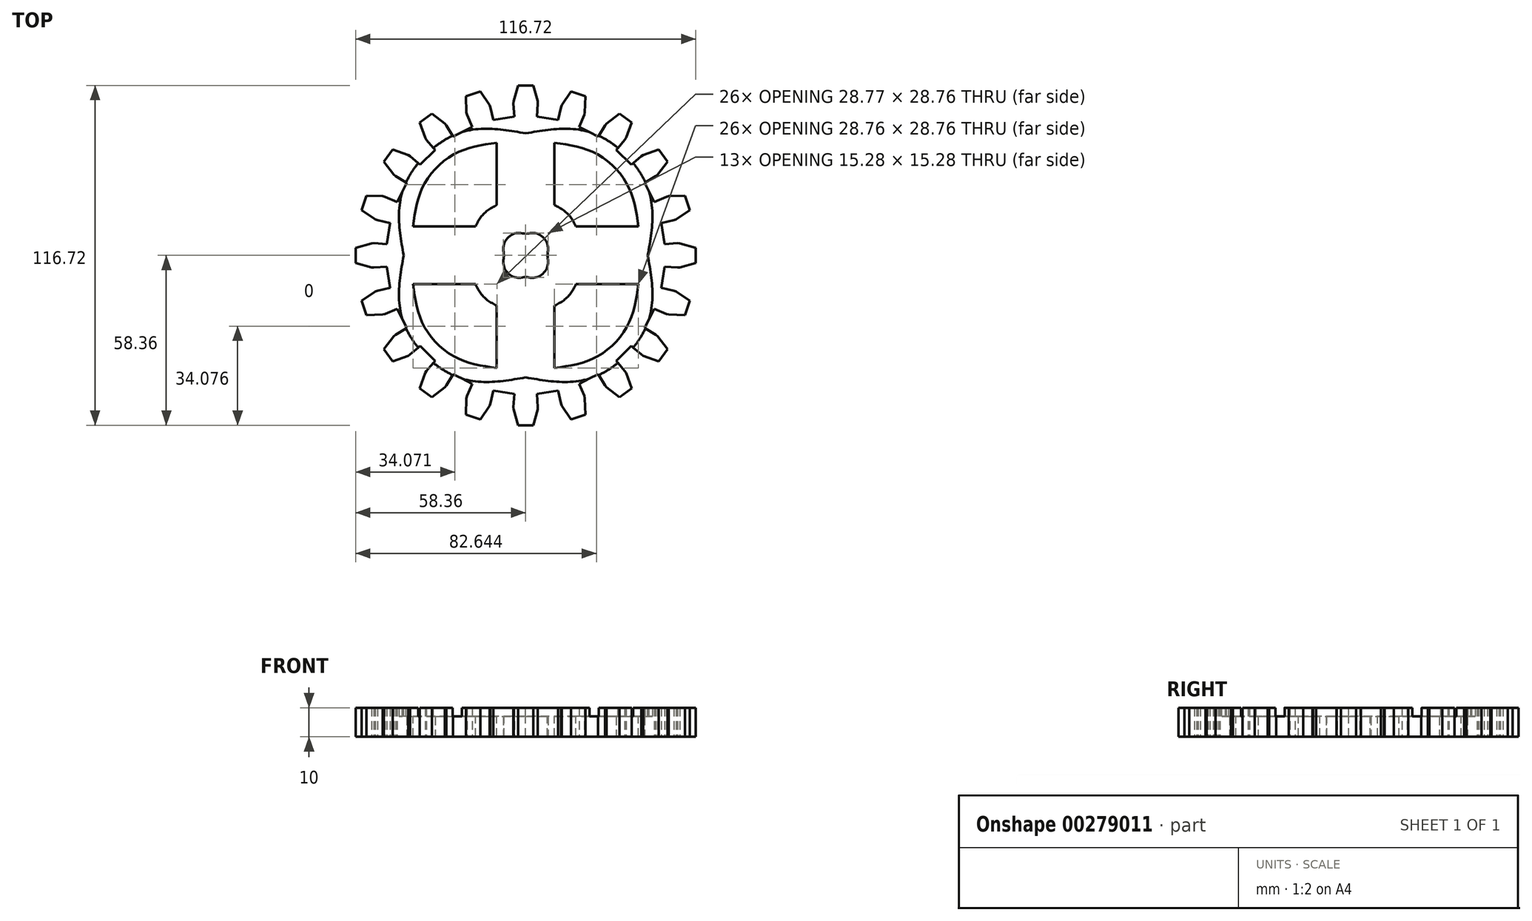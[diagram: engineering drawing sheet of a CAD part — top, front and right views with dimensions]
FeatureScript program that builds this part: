
annotation { "Feature Type Name" : "Feature", "Feature Type Description" : "" }
export const myFeature = defineFeature(function(context is Context, id is Id, definition is map)
    precondition{}
    {
        {
            var Q0;
            Q0=qCreatedBy(makeId("Top.planeOp"),FACE);
            var sketch = newSketch(context, id + "F0", { "sketchPlane" : qUnion([Q0])});
            skLineSegment(sketch, "E0", {"start": v(-2.6, 58.36) * mm, "end": v(-4.17, 52.94) * mm});
            skLineSegment(sketch, "E1", {"start": v(-4.17, 52.94) * mm, "end": v(-4.2, 52.13) * mm});
            skLineSegment(sketch, "E2", {"start": v(-4.2, 52.13) * mm, "end": v(-3.84, 47.64) * mm});
            skLineSegment(sketch, "E3", {"start": v(-3.84, 47.64) * mm, "end": v(-11.08, 46.5) * mm});
            skLineSegment(sketch, "E4", {"start": v(-11.08, 46.5) * mm, "end": v(-12.12, 50.88) * mm});
            skLineSegment(sketch, "E5", {"start": v(-12.12, 50.88) * mm, "end": v(-12.4, 51.64) * mm});
            skLineSegment(sketch, "E6", {"start": v(-12.4, 51.64) * mm, "end": v(-15.57, 56.3) * mm});
            skLineSegment(sketch, "E7", {"start": v(-15.57, 56.3) * mm, "end": v(-20.5, 54.7) * mm});
            skLineSegment(sketch, "E8", {"start": v(-20.5, 54.7) * mm, "end": v(-20.33, 49.06) * mm});
            skLineSegment(sketch, "E9", {"start": v(-20.33, 49.06) * mm, "end": v(-20.1, 48.29) * mm});
            skLineSegment(sketch, "E10", {"start": v(-20.1, 48.29) * mm, "end": v(-18.37, 44.12) * mm});
            skLineSegment(sketch, "E11", {"start": v(-18.37, 44.12) * mm, "end": v(-24.9, 40.8) * mm});
            skLineSegment(sketch, "E12", {"start": v(-24.9, 40.8) * mm, "end": v(-27.25, 44.64) * mm});
            skLineSegment(sketch, "E13", {"start": v(-27.25, 44.64) * mm, "end": v(-27.75, 45.28) * mm});
            skLineSegment(sketch, "E14", {"start": v(-27.75, 45.28) * mm, "end": v(-32.2, 48.74) * mm});
            skLineSegment(sketch, "E15", {"start": v(-32.2, 48.74) * mm, "end": v(-36.4, 45.68) * mm});
            skLineSegment(sketch, "E16", {"start": v(-36.4, 45.68) * mm, "end": v(-34.5, 40.38) * mm});
            skLineSegment(sketch, "E17", {"start": v(-34.5, 40.38) * mm, "end": v(-34.04, 39.7) * mm});
            skLineSegment(sketch, "E18", {"start": v(-34.04, 39.7) * mm, "end": v(-31.1, 36.3) * mm});
            skLineSegment(sketch, "E19", {"start": v(-31.1, 36.3) * mm, "end": v(-36.3, 31.1) * mm});
            skLineSegment(sketch, "E20", {"start": v(-36.3, 31.1) * mm, "end": v(-39.71, 34.03) * mm});
            skLineSegment(sketch, "E21", {"start": v(-39.71, 34.03) * mm, "end": v(-40.38, 34.5) * mm});
            skLineSegment(sketch, "E22", {"start": v(-40.38, 34.5) * mm, "end": v(-45.7, 36.4) * mm});
            skLineSegment(sketch, "E23", {"start": v(-45.7, 36.4) * mm, "end": v(-48.75, 32.2) * mm});
            skLineSegment(sketch, "E24", {"start": v(-48.75, 32.2) * mm, "end": v(-45.29, 27.75) * mm});
            skLineSegment(sketch, "E25", {"start": v(-45.29, 27.75) * mm, "end": v(-44.64, 27.24) * mm});
            skLineSegment(sketch, "E26", {"start": v(-44.64, 27.24) * mm, "end": v(-40.8, 24.9) * mm});
            skLineSegment(sketch, "E27", {"start": v(-40.8, 24.9) * mm, "end": v(-44.12, 18.37) * mm});
            skLineSegment(sketch, "E28", {"start": v(-44.12, 18.37) * mm, "end": v(-48.29, 20.1) * mm});
            skLineSegment(sketch, "E29", {"start": v(-48.29, 20.1) * mm, "end": v(-49.07, 20.32) * mm});
            skLineSegment(sketch, "E30", {"start": v(-49.07, 20.32) * mm, "end": v(-54.7, 20.5) * mm});
            skLineSegment(sketch, "E31", {"start": v(-54.7, 20.5) * mm, "end": v(-56.31, 15.57) * mm});
            skLineSegment(sketch, "E32", {"start": v(-56.31, 15.57) * mm, "end": v(-51.65, 12.4) * mm});
            skLineSegment(sketch, "E33", {"start": v(-51.65, 12.4) * mm, "end": v(-50.88, 12.12) * mm});
            skLineSegment(sketch, "E34", {"start": v(-50.88, 12.12) * mm, "end": v(-46.5, 11.08) * mm});
            skLineSegment(sketch, "E35", {"start": v(-46.5, 11.08) * mm, "end": v(-47.64, 3.84) * mm});
            skLineSegment(sketch, "E36", {"start": v(-47.64, 3.84) * mm, "end": v(-52.13, 4.2) * mm});
            skLineSegment(sketch, "E37", {"start": v(-52.13, 4.2) * mm, "end": v(-52.94, 4.16) * mm});
            skLineSegment(sketch, "E38", {"start": v(-52.94, 4.16) * mm, "end": v(-58.36, 2.6) * mm});
            skLineSegment(sketch, "E39", {"start": v(-58.36, 2.6) * mm, "end": v(-58.36, -2.6) * mm});
            skLineSegment(sketch, "E40", {"start": v(-58.36, -2.6) * mm, "end": v(-52.94, -4.16) * mm});
            skLineSegment(sketch, "E41", {"start": v(-52.94, -4.16) * mm, "end": v(-52.13, -4.2) * mm});
            skLineSegment(sketch, "E42", {"start": v(-52.13, -4.2) * mm, "end": v(-47.64, -3.84) * mm});
            skLineSegment(sketch, "E43", {"start": v(-47.64, -3.84) * mm, "end": v(-46.5, -11.08) * mm});
            skLineSegment(sketch, "E44", {"start": v(-46.5, -11.08) * mm, "end": v(-50.88, -12.12) * mm});
            skLineSegment(sketch, "E45", {"start": v(-50.88, -12.12) * mm, "end": v(-51.65, -12.4) * mm});
            skLineSegment(sketch, "E46", {"start": v(-51.65, -12.4) * mm, "end": v(-56.31, -15.57) * mm});
            skLineSegment(sketch, "E47", {"start": v(-56.31, -15.57) * mm, "end": v(-54.7, -20.5) * mm});
            skLineSegment(sketch, "E48", {"start": v(-54.7, -20.5) * mm, "end": v(-49.07, -20.32) * mm});
            skLineSegment(sketch, "E49", {"start": v(-49.07, -20.32) * mm, "end": v(-48.29, -20.1) * mm});
            skLineSegment(sketch, "E50", {"start": v(-48.29, -20.1) * mm, "end": v(-44.12, -18.37) * mm});
            skLineSegment(sketch, "E51", {"start": v(-44.12, -18.37) * mm, "end": v(-40.8, -24.9) * mm});
            skLineSegment(sketch, "E52", {"start": v(-40.8, -24.9) * mm, "end": v(-44.64, -27.24) * mm});
            skLineSegment(sketch, "E53", {"start": v(-44.64, -27.24) * mm, "end": v(-45.29, -27.75) * mm});
            skLineSegment(sketch, "E54", {"start": v(-45.29, -27.75) * mm, "end": v(-48.75, -32.2) * mm});
            skLineSegment(sketch, "E55", {"start": v(-48.75, -32.2) * mm, "end": v(-45.7, -36.4) * mm});
            skLineSegment(sketch, "E56", {"start": v(-45.7, -36.4) * mm, "end": v(-40.38, -34.5) * mm});
            skLineSegment(sketch, "E57", {"start": v(-40.38, -34.5) * mm, "end": v(-39.71, -34.03) * mm});
            skLineSegment(sketch, "E58", {"start": v(-39.71, -34.03) * mm, "end": v(-36.3, -31.1) * mm});
            skLineSegment(sketch, "E59", {"start": v(-36.3, -31.1) * mm, "end": v(-31.1, -36.3) * mm});
            skLineSegment(sketch, "E60", {"start": v(-31.1, -36.3) * mm, "end": v(-34.04, -39.7) * mm});
            skLineSegment(sketch, "E61", {"start": v(-34.04, -39.7) * mm, "end": v(-34.5, -40.38) * mm});
            skLineSegment(sketch, "E62", {"start": v(-34.5, -40.38) * mm, "end": v(-36.4, -45.68) * mm});
            skLineSegment(sketch, "E63", {"start": v(-36.4, -45.68) * mm, "end": v(-32.2, -48.74) * mm});
            skLineSegment(sketch, "E64", {"start": v(-32.2, -48.74) * mm, "end": v(-27.75, -45.28) * mm});
            skLineSegment(sketch, "E65", {"start": v(-27.75, -45.28) * mm, "end": v(-27.25, -44.64) * mm});
            skLineSegment(sketch, "E66", {"start": v(-27.25, -44.64) * mm, "end": v(-24.9, -40.8) * mm});
            skLineSegment(sketch, "E67", {"start": v(-24.9, -40.8) * mm, "end": v(-18.37, -44.12) * mm});
            skLineSegment(sketch, "E68", {"start": v(-18.37, -44.12) * mm, "end": v(-20.1, -48.28) * mm});
            skLineSegment(sketch, "E69", {"start": v(-20.1, -48.28) * mm, "end": v(-20.33, -49.06) * mm});
            skLineSegment(sketch, "E70", {"start": v(-20.33, -49.06) * mm, "end": v(-20.5, -54.7) * mm});
            skLineSegment(sketch, "E71", {"start": v(-20.5, -54.7) * mm, "end": v(-15.57, -56.3) * mm});
            skLineSegment(sketch, "E72", {"start": v(-15.57, -56.3) * mm, "end": v(-12.4, -51.64) * mm});
            skLineSegment(sketch, "E73", {"start": v(-12.4, -51.64) * mm, "end": v(-12.12, -50.88) * mm});
            skLineSegment(sketch, "E74", {"start": v(-12.12, -50.88) * mm, "end": v(-11.08, -46.5) * mm});
            skLineSegment(sketch, "E75", {"start": v(-11.08, -46.5) * mm, "end": v(-3.84, -47.64) * mm});
            skLineSegment(sketch, "E76", {"start": v(-3.84, -47.64) * mm, "end": v(-4.2, -52.13) * mm});
            skLineSegment(sketch, "E77", {"start": v(-4.2, -52.13) * mm, "end": v(-4.17, -52.94) * mm});
            skLineSegment(sketch, "E78", {"start": v(-4.17, -52.94) * mm, "end": v(-2.6, -58.36) * mm});
            skLineSegment(sketch, "E79", {"start": v(-2.6, -58.36) * mm, "end": v(2.6, -58.36) * mm});
            skLineSegment(sketch, "E80", {"start": v(2.6, -58.36) * mm, "end": v(4.16, -52.94) * mm});
            skLineSegment(sketch, "E81", {"start": v(4.16, -52.94) * mm, "end": v(4.19, -52.13) * mm});
            skLineSegment(sketch, "E82", {"start": v(4.19, -52.13) * mm, "end": v(3.83, -47.64) * mm});
            skLineSegment(sketch, "E83", {"start": v(3.83, -47.64) * mm, "end": v(11.07, -46.5) * mm});
            skLineSegment(sketch, "E84", {"start": v(11.07, -46.5) * mm, "end": v(12.12, -50.88) * mm});
            skLineSegment(sketch, "E85", {"start": v(12.12, -50.88) * mm, "end": v(12.4, -51.64) * mm});
            skLineSegment(sketch, "E86", {"start": v(12.4, -51.64) * mm, "end": v(15.56, -56.3) * mm});
            skLineSegment(sketch, "E87", {"start": v(15.56, -56.3) * mm, "end": v(20.5, -54.7) * mm});
            skLineSegment(sketch, "E88", {"start": v(20.5, -54.7) * mm, "end": v(20.32, -49.06) * mm});
            skLineSegment(sketch, "E89", {"start": v(20.32, -49.06) * mm, "end": v(20.1, -48.28) * mm});
            skLineSegment(sketch, "E90", {"start": v(20.1, -48.28) * mm, "end": v(18.36, -44.12) * mm});
            skLineSegment(sketch, "E91", {"start": v(18.36, -44.12) * mm, "end": v(24.9, -40.8) * mm});
            skLineSegment(sketch, "E92", {"start": v(24.9, -40.8) * mm, "end": v(27.24, -44.64) * mm});
            skLineSegment(sketch, "E93", {"start": v(27.24, -44.64) * mm, "end": v(27.75, -45.28) * mm});
            skLineSegment(sketch, "E94", {"start": v(27.75, -45.28) * mm, "end": v(32.2, -48.74) * mm});
            skLineSegment(sketch, "E95", {"start": v(32.2, -48.74) * mm, "end": v(36.4, -45.68) * mm});
            skLineSegment(sketch, "E96", {"start": v(36.4, -45.68) * mm, "end": v(34.48, -40.38) * mm});
            skLineSegment(sketch, "E97", {"start": v(34.48, -40.38) * mm, "end": v(34.03, -39.7) * mm});
            skLineSegment(sketch, "E98", {"start": v(34.03, -39.7) * mm, "end": v(31.1, -36.3) * mm});
            skLineSegment(sketch, "E99", {"start": v(31.1, -36.3) * mm, "end": v(36.28, -31.1) * mm});
            skLineSegment(sketch, "E100", {"start": v(36.28, -31.1) * mm, "end": v(39.7, -34.03) * mm});
            skLineSegment(sketch, "E101", {"start": v(39.7, -34.03) * mm, "end": v(40.38, -34.5) * mm});
            skLineSegment(sketch, "E102", {"start": v(40.38, -34.5) * mm, "end": v(45.68, -36.4) * mm});
            skLineSegment(sketch, "E103", {"start": v(45.68, -36.4) * mm, "end": v(48.74, -32.2) * mm});
            skLineSegment(sketch, "E104", {"start": v(48.74, -32.2) * mm, "end": v(45.28, -27.75) * mm});
            skLineSegment(sketch, "E105", {"start": v(45.28, -27.75) * mm, "end": v(44.64, -27.24) * mm});
            skLineSegment(sketch, "E106", {"start": v(44.64, -27.24) * mm, "end": v(40.79, -24.9) * mm});
            skLineSegment(sketch, "E107", {"start": v(40.79, -24.9) * mm, "end": v(44.12, -18.37) * mm});
            skLineSegment(sketch, "E108", {"start": v(44.12, -18.37) * mm, "end": v(48.28, -20.1) * mm});
            skLineSegment(sketch, "E109", {"start": v(48.28, -20.1) * mm, "end": v(49.06, -20.32) * mm});
            skLineSegment(sketch, "E110", {"start": v(49.06, -20.32) * mm, "end": v(54.7, -20.5) * mm});
            skLineSegment(sketch, "E111", {"start": v(54.7, -20.5) * mm, "end": v(56.3, -15.57) * mm});
            skLineSegment(sketch, "E112", {"start": v(56.3, -15.57) * mm, "end": v(51.64, -12.4) * mm});
            skLineSegment(sketch, "E113", {"start": v(51.64, -12.4) * mm, "end": v(50.87, -12.12) * mm});
            skLineSegment(sketch, "E114", {"start": v(50.87, -12.12) * mm, "end": v(46.49, -11.08) * mm});
            skLineSegment(sketch, "E115", {"start": v(46.49, -11.08) * mm, "end": v(47.63, -3.84) * mm});
            skLineSegment(sketch, "E116", {"start": v(47.63, -3.84) * mm, "end": v(52.12, -4.2) * mm});
            skLineSegment(sketch, "E117", {"start": v(52.12, -4.2) * mm, "end": v(52.94, -4.16) * mm});
            skLineSegment(sketch, "E118", {"start": v(52.94, -4.16) * mm, "end": v(58.36, -2.6) * mm});
            skLineSegment(sketch, "E119", {"start": v(58.36, -2.6) * mm, "end": v(58.36, 2.6) * mm});
            skLineSegment(sketch, "E120", {"start": v(58.36, 2.6) * mm, "end": v(52.94, 4.16) * mm});
            skLineSegment(sketch, "E121", {"start": v(52.94, 4.16) * mm, "end": v(52.12, 4.2) * mm});
            skLineSegment(sketch, "E122", {"start": v(52.12, 4.2) * mm, "end": v(47.63, 3.84) * mm});
            skLineSegment(sketch, "E123", {"start": v(47.63, 3.84) * mm, "end": v(46.49, 11.08) * mm});
            skLineSegment(sketch, "E124", {"start": v(46.49, 11.08) * mm, "end": v(50.87, 12.12) * mm});
            skLineSegment(sketch, "E125", {"start": v(50.87, 12.12) * mm, "end": v(51.64, 12.4) * mm});
            skLineSegment(sketch, "E126", {"start": v(51.64, 12.4) * mm, "end": v(56.3, 15.57) * mm});
            skLineSegment(sketch, "E127", {"start": v(56.3, 15.57) * mm, "end": v(54.7, 20.5) * mm});
            skLineSegment(sketch, "E128", {"start": v(54.7, 20.5) * mm, "end": v(49.06, 20.32) * mm});
            skLineSegment(sketch, "E129", {"start": v(49.06, 20.32) * mm, "end": v(48.28, 20.1) * mm});
            skLineSegment(sketch, "E130", {"start": v(48.28, 20.1) * mm, "end": v(44.12, 18.37) * mm});
            skLineSegment(sketch, "E131", {"start": v(44.12, 18.37) * mm, "end": v(40.79, 24.9) * mm});
            skLineSegment(sketch, "E132", {"start": v(40.79, 24.9) * mm, "end": v(44.64, 27.24) * mm});
            skLineSegment(sketch, "E133", {"start": v(44.64, 27.24) * mm, "end": v(45.28, 27.75) * mm});
            skLineSegment(sketch, "E134", {"start": v(45.28, 27.75) * mm, "end": v(48.74, 32.2) * mm});
            skLineSegment(sketch, "E135", {"start": v(48.74, 32.2) * mm, "end": v(45.68, 36.4) * mm});
            skLineSegment(sketch, "E136", {"start": v(45.68, 36.4) * mm, "end": v(40.38, 34.5) * mm});
            skLineSegment(sketch, "E137", {"start": v(40.38, 34.5) * mm, "end": v(39.7, 34.03) * mm});
            skLineSegment(sketch, "E138", {"start": v(39.7, 34.03) * mm, "end": v(36.28, 31.1) * mm});
            skLineSegment(sketch, "E139", {"start": v(36.28, 31.1) * mm, "end": v(31.1, 36.3) * mm});
            skLineSegment(sketch, "E140", {"start": v(31.1, 36.3) * mm, "end": v(34.03, 39.7) * mm});
            skLineSegment(sketch, "E141", {"start": v(34.03, 39.7) * mm, "end": v(34.48, 40.38) * mm});
            skLineSegment(sketch, "E142", {"start": v(34.48, 40.38) * mm, "end": v(36.4, 45.68) * mm});
            skLineSegment(sketch, "E143", {"start": v(36.4, 45.68) * mm, "end": v(32.2, 48.74) * mm});
            skLineSegment(sketch, "E144", {"start": v(32.2, 48.74) * mm, "end": v(27.75, 45.28) * mm});
            skLineSegment(sketch, "E145", {"start": v(27.75, 45.28) * mm, "end": v(27.24, 44.64) * mm});
            skLineSegment(sketch, "E146", {"start": v(27.24, 44.64) * mm, "end": v(24.9, 40.8) * mm});
            skLineSegment(sketch, "E147", {"start": v(24.9, 40.8) * mm, "end": v(18.36, 44.12) * mm});
            skLineSegment(sketch, "E148", {"start": v(18.36, 44.12) * mm, "end": v(20.1, 48.29) * mm});
            skLineSegment(sketch, "E149", {"start": v(20.1, 48.29) * mm, "end": v(20.32, 49.06) * mm});
            skLineSegment(sketch, "E150", {"start": v(20.32, 49.06) * mm, "end": v(20.5, 54.7) * mm});
            skLineSegment(sketch, "E151", {"start": v(20.5, 54.7) * mm, "end": v(15.56, 56.3) * mm});
            skLineSegment(sketch, "E152", {"start": v(15.56, 56.3) * mm, "end": v(12.4, 51.64) * mm});
            skLineSegment(sketch, "E153", {"start": v(12.4, 51.64) * mm, "end": v(12.12, 50.88) * mm});
            skLineSegment(sketch, "E154", {"start": v(12.12, 50.88) * mm, "end": v(11.07, 46.5) * mm});
            skLineSegment(sketch, "E155", {"start": v(11.07, 46.5) * mm, "end": v(3.83, 47.64) * mm});
            skLineSegment(sketch, "E156", {"start": v(3.83, 47.64) * mm, "end": v(4.19, 52.13) * mm});
            skLineSegment(sketch, "E157", {"start": v(4.19, 52.13) * mm, "end": v(4.16, 52.94) * mm});
            skLineSegment(sketch, "E158", {"start": v(4.16, 52.94) * mm, "end": v(2.6, 58.36) * mm});
            skLineSegment(sketch, "E159", {"start": v(2.6, 58.36) * mm, "end": v(-2.6, 58.36) * mm});
            skSolve(sketch);
        }
        {
            var Q0;
            Q0 = qSketchRegion(id + "F0", true);
            extrude(context, id + "F1", {"entities" : qUnion([Q0]), "depth" : 10 * mm});
        }
        {
            var Q0;
            Q0=makeQuery(id+"F1.opExtrude","CAP_FACE",FACE,{"disambiguationData":[OSD([sQuery(id+"F0.wireOp",EDGE,"E0"),sQuery(id+"F0.wireOp",EDGE,"E1"),sQuery(id+"F0.wireOp",EDGE,"E2"),sQuery(id+"F0.wireOp",EDGE,"E3"),sQuery(id+"F0.wireOp",EDGE,"E4"),sQuery(id+"F0.wireOp",EDGE,"E5"),sQuery(id+"F0.wireOp",EDGE,"E6"),sQuery(id+"F0.wireOp",EDGE,"E7"),sQuery(id+"F0.wireOp",EDGE,"E8"),sQuery(id+"F0.wireOp",EDGE,"E9"),sQuery(id+"F0.wireOp",EDGE,"E10"),sQuery(id+"F0.wireOp",EDGE,"E11"),sQuery(id+"F0.wireOp",EDGE,"E12"),sQuery(id+"F0.wireOp",EDGE,"E13"),sQuery(id+"F0.wireOp",EDGE,"E14"),sQuery(id+"F0.wireOp",EDGE,"E15"),sQuery(id+"F0.wireOp",EDGE,"E16"),sQuery(id+"F0.wireOp",EDGE,"E17"),sQuery(id+"F0.wireOp",EDGE,"E18"),sQuery(id+"F0.wireOp",EDGE,"E19"),sQuery(id+"F0.wireOp",EDGE,"E20"),sQuery(id+"F0.wireOp",EDGE,"E21"),sQuery(id+"F0.wireOp",EDGE,"E22"),sQuery(id+"F0.wireOp",EDGE,"E23"),sQuery(id+"F0.wireOp",EDGE,"E24"),sQuery(id+"F0.wireOp",EDGE,"E25"),sQuery(id+"F0.wireOp",EDGE,"E26"),sQuery(id+"F0.wireOp",EDGE,"E27"),sQuery(id+"F0.wireOp",EDGE,"E28"),sQuery(id+"F0.wireOp",EDGE,"E29"),sQuery(id+"F0.wireOp",EDGE,"E30"),sQuery(id+"F0.wireOp",EDGE,"E31"),sQuery(id+"F0.wireOp",EDGE,"E32"),sQuery(id+"F0.wireOp",EDGE,"E33"),sQuery(id+"F0.wireOp",EDGE,"E34"),sQuery(id+"F0.wireOp",EDGE,"E35"),sQuery(id+"F0.wireOp",EDGE,"E36"),sQuery(id+"F0.wireOp",EDGE,"E37"),sQuery(id+"F0.wireOp",EDGE,"E38"),sQuery(id+"F0.wireOp",EDGE,"E39"),sQuery(id+"F0.wireOp",EDGE,"E40"),sQuery(id+"F0.wireOp",EDGE,"E41"),sQuery(id+"F0.wireOp",EDGE,"E42"),sQuery(id+"F0.wireOp",EDGE,"E43"),sQuery(id+"F0.wireOp",EDGE,"E44"),sQuery(id+"F0.wireOp",EDGE,"E45"),sQuery(id+"F0.wireOp",EDGE,"E46"),sQuery(id+"F0.wireOp",EDGE,"E47"),sQuery(id+"F0.wireOp",EDGE,"E48"),sQuery(id+"F0.wireOp",EDGE,"E49"),sQuery(id+"F0.wireOp",EDGE,"E50"),sQuery(id+"F0.wireOp",EDGE,"E51"),sQuery(id+"F0.wireOp",EDGE,"E52"),sQuery(id+"F0.wireOp",EDGE,"E53"),sQuery(id+"F0.wireOp",EDGE,"E54"),sQuery(id+"F0.wireOp",EDGE,"E55"),sQuery(id+"F0.wireOp",EDGE,"E56"),sQuery(id+"F0.wireOp",EDGE,"E57"),sQuery(id+"F0.wireOp",EDGE,"E58"),sQuery(id+"F0.wireOp",EDGE,"E59"),sQuery(id+"F0.wireOp",EDGE,"E60"),sQuery(id+"F0.wireOp",EDGE,"E61"),sQuery(id+"F0.wireOp",EDGE,"E62"),sQuery(id+"F0.wireOp",EDGE,"E63"),sQuery(id+"F0.wireOp",EDGE,"E64"),sQuery(id+"F0.wireOp",EDGE,"E65"),sQuery(id+"F0.wireOp",EDGE,"E66"),sQuery(id+"F0.wireOp",EDGE,"E67"),sQuery(id+"F0.wireOp",EDGE,"E68"),sQuery(id+"F0.wireOp",EDGE,"E69"),sQuery(id+"F0.wireOp",EDGE,"E70"),sQuery(id+"F0.wireOp",EDGE,"E71"),sQuery(id+"F0.wireOp",EDGE,"E72"),sQuery(id+"F0.wireOp",EDGE,"E73"),sQuery(id+"F0.wireOp",EDGE,"E74"),sQuery(id+"F0.wireOp",EDGE,"E75"),sQuery(id+"F0.wireOp",EDGE,"E76"),sQuery(id+"F0.wireOp",EDGE,"E77"),sQuery(id+"F0.wireOp",EDGE,"E78"),sQuery(id+"F0.wireOp",EDGE,"E79"),sQuery(id+"F0.wireOp",EDGE,"E80"),sQuery(id+"F0.wireOp",EDGE,"E81"),sQuery(id+"F0.wireOp",EDGE,"E82"),sQuery(id+"F0.wireOp",EDGE,"E83"),sQuery(id+"F0.wireOp",EDGE,"E84"),sQuery(id+"F0.wireOp",EDGE,"E85"),sQuery(id+"F0.wireOp",EDGE,"E86"),sQuery(id+"F0.wireOp",EDGE,"E87"),sQuery(id+"F0.wireOp",EDGE,"E88"),sQuery(id+"F0.wireOp",EDGE,"E89"),sQuery(id+"F0.wireOp",EDGE,"E90"),sQuery(id+"F0.wireOp",EDGE,"E91"),sQuery(id+"F0.wireOp",EDGE,"E92"),sQuery(id+"F0.wireOp",EDGE,"E93"),sQuery(id+"F0.wireOp",EDGE,"E94"),sQuery(id+"F0.wireOp",EDGE,"E95"),sQuery(id+"F0.wireOp",EDGE,"E96"),sQuery(id+"F0.wireOp",EDGE,"E97"),sQuery(id+"F0.wireOp",EDGE,"E98"),sQuery(id+"F0.wireOp",EDGE,"E99"),sQuery(id+"F0.wireOp",EDGE,"E100"),sQuery(id+"F0.wireOp",EDGE,"E101"),sQuery(id+"F0.wireOp",EDGE,"E102"),sQuery(id+"F0.wireOp",EDGE,"E103"),sQuery(id+"F0.wireOp",EDGE,"E104"),sQuery(id+"F0.wireOp",EDGE,"E105"),sQuery(id+"F0.wireOp",EDGE,"E106"),sQuery(id+"F0.wireOp",EDGE,"E107"),sQuery(id+"F0.wireOp",EDGE,"E108"),sQuery(id+"F0.wireOp",EDGE,"E109"),sQuery(id+"F0.wireOp",EDGE,"E110"),sQuery(id+"F0.wireOp",EDGE,"E111"),sQuery(id+"F0.wireOp",EDGE,"E112"),sQuery(id+"F0.wireOp",EDGE,"E113"),sQuery(id+"F0.wireOp",EDGE,"E114"),sQuery(id+"F0.wireOp",EDGE,"E115"),sQuery(id+"F0.wireOp",EDGE,"E116"),sQuery(id+"F0.wireOp",EDGE,"E117"),sQuery(id+"F0.wireOp",EDGE,"E118"),sQuery(id+"F0.wireOp",EDGE,"E119"),sQuery(id+"F0.wireOp",EDGE,"E120"),sQuery(id+"F0.wireOp",EDGE,"E121"),sQuery(id+"F0.wireOp",EDGE,"E122"),sQuery(id+"F0.wireOp",EDGE,"E123"),sQuery(id+"F0.wireOp",EDGE,"E124"),sQuery(id+"F0.wireOp",EDGE,"E125"),sQuery(id+"F0.wireOp",EDGE,"E126"),sQuery(id+"F0.wireOp",EDGE,"E127"),sQuery(id+"F0.wireOp",EDGE,"E128"),sQuery(id+"F0.wireOp",EDGE,"E129"),sQuery(id+"F0.wireOp",EDGE,"E130"),sQuery(id+"F0.wireOp",EDGE,"E131"),sQuery(id+"F0.wireOp",EDGE,"E132"),sQuery(id+"F0.wireOp",EDGE,"E133"),sQuery(id+"F0.wireOp",EDGE,"E134"),sQuery(id+"F0.wireOp",EDGE,"E135"),sQuery(id+"F0.wireOp",EDGE,"E136"),sQuery(id+"F0.wireOp",EDGE,"E137"),sQuery(id+"F0.wireOp",EDGE,"E138"),sQuery(id+"F0.wireOp",EDGE,"E139"),sQuery(id+"F0.wireOp",EDGE,"E140"),sQuery(id+"F0.wireOp",EDGE,"E141"),sQuery(id+"F0.wireOp",EDGE,"E142"),sQuery(id+"F0.wireOp",EDGE,"E143"),sQuery(id+"F0.wireOp",EDGE,"E144"),sQuery(id+"F0.wireOp",EDGE,"E145"),sQuery(id+"F0.wireOp",EDGE,"E146"),sQuery(id+"F0.wireOp",EDGE,"E147"),sQuery(id+"F0.wireOp",EDGE,"E148"),sQuery(id+"F0.wireOp",EDGE,"E149"),sQuery(id+"F0.wireOp",EDGE,"E150"),sQuery(id+"F0.wireOp",EDGE,"E151"),sQuery(id+"F0.wireOp",EDGE,"E152"),sQuery(id+"F0.wireOp",EDGE,"E153"),sQuery(id+"F0.wireOp",EDGE,"E154"),sQuery(id+"F0.wireOp",EDGE,"E155"),sQuery(id+"F0.wireOp",EDGE,"E156"),sQuery(id+"F0.wireOp",EDGE,"E157"),sQuery(id+"F0.wireOp",EDGE,"E158"),sQuery(id+"F0.wireOp",EDGE,"E159")])],"isStart":false});
            var sketch = newSketch(context, id + "F2", { "sketchPlane" : qUnion([Q0])});
            skFitSpline(sketch, "E160", {"points": [v(41.9, 0) * mm, v(41.9, -23.14) * mm, v(23.14, -41.9) * mm, v(0, -41.9) * mm]});
            skFitSpline(sketch, "E161", {"points": [v(0, -41.9) * mm, v(-23.14, -41.9) * mm, v(-41.9, -23.14) * mm, v(-41.9, 0) * mm]});
            skFitSpline(sketch, "E162", {"points": [v(-41.9, 0) * mm, v(-41.9, 23.14) * mm, v(-23.14, 41.9) * mm, v(0, 41.9) * mm]});
            skFitSpline(sketch, "E163", {"points": [v(0, 41.9) * mm, v(23.14, 41.9) * mm, v(41.9, 23.14) * mm, v(41.9, 0) * mm]});
            skSolve(sketch);
        }
        {
            var Q0;
            Q0 = qSketchRegion(id + "F2", true);
            extrude(context, id + "F3", {"entities" : qUnion([Q0]), "operationType" : NewBodyOperationType.REMOVE, "oppositeDirection" : true, "depth" : 3 * mm});
        }
        {
            var Q0;
            Q0=makeQuery(id+"F3.boolean.opBoolean","COPY",FACE,{"derivedFrom":makeQuery(id+"F3.opExtrude","CAP_FACE",FACE,{"disambiguationData":[OSD([sQuery(id+"F2.wireOp",EDGE,"E160"),sQuery(id+"F2.wireOp",EDGE,"E161"),sQuery(id+"F2.wireOp",EDGE,"E162"),sQuery(id+"F2.wireOp",EDGE,"E163")])],"isStart":false})});
            var sketch = newSketch(context, id + "F4", { "sketchPlane" : qUnion([Q0])});
            skFitSpline(sketch, "E164", {"points": [v(-9.9, 17.26) * mm, v(-12.96, 15.5) * mm, v(-15.5, 12.96) * mm, v(-17.26, 9.9) * mm]});
            skLineSegment(sketch, "E165", {"start": v(-9.9, 38.66) * mm, "end": v(-9.9, 17.26) * mm});
            skLineSegment(sketch, "E166", {"start": v(-9.9, 17.26) * mm, "end": v(-9.9, 38.66) * mm});
            skFitSpline(sketch, "E167", {"points": [v(-38.67, 9.9) * mm, v(-35.08, 23.98) * mm, v(-23.99, 35.07) * mm, v(-9.9, 38.66) * mm]});
            skLineSegment(sketch, "E168", {"start": v(-17.26, 9.9) * mm, "end": v(-38.67, 9.9) * mm});
            skLineSegment(sketch, "E169", {"start": v(-38.67, 9.9) * mm, "end": v(-17.26, 9.9) * mm});
            skFitSpline(sketch, "E170", {"points": [v(9.9, 38.66) * mm, v(23.98, 35.07) * mm, v(35.07, 23.98) * mm, v(38.66, 9.9) * mm]});
            skFitSpline(sketch, "E171", {"points": [v(17.26, 9.9) * mm, v(15.5, 12.96) * mm, v(12.96, 15.5) * mm, v(9.9, 17.26) * mm]});
            skLineSegment(sketch, "E172", {"start": v(38.66, 9.9) * mm, "end": v(17.26, 9.9) * mm});
            skLineSegment(sketch, "E173", {"start": v(17.26, 9.9) * mm, "end": v(38.66, 9.9) * mm});
            skFitSpline(sketch, "E174", {"points": [v(0, 7.4) * mm, v(4.09, 7.4) * mm, v(7.4, 4.09) * mm, v(7.4, 0) * mm]});
            skFitSpline(sketch, "E175", {"points": [v(7.4, 0) * mm, v(7.4, -4.09) * mm, v(4.09, -7.4) * mm, v(0, -7.4) * mm]});
            skFitSpline(sketch, "E176", {"points": [v(0, -7.4) * mm, v(-4.09, -7.4) * mm, v(-7.4, -4.09) * mm, v(-7.4, 0) * mm]});
            skFitSpline(sketch, "E177", {"points": [v(-7.4, 0) * mm, v(-7.4, 4.09) * mm, v(-4.09, 7.4) * mm, v(0, 7.4) * mm]});
            skLineSegment(sketch, "E178", {"start": v(9.9, 17.26) * mm, "end": v(9.9, 38.66) * mm});
            skLineSegment(sketch, "E179", {"start": v(9.9, 38.66) * mm, "end": v(9.9, 17.26) * mm});
            skFitSpline(sketch, "E180", {"points": [v(-17.26, -9.9) * mm, v(-15.5, -12.96) * mm, v(-12.96, -15.5) * mm, v(-9.9, -17.26) * mm]});
            skLineSegment(sketch, "E181", {"start": v(-38.67, -9.9) * mm, "end": v(-17.26, -9.9) * mm});
            skLineSegment(sketch, "E182", {"start": v(-17.26, -9.9) * mm, "end": v(-38.67, -9.9) * mm});
            skFitSpline(sketch, "E183", {"points": [v(-9.9, -38.66) * mm, v(-23.99, -35.07) * mm, v(-35.08, -23.98) * mm, v(-38.67, -9.9) * mm]});
            skLineSegment(sketch, "E184", {"start": v(-9.9, -17.26) * mm, "end": v(-9.9, -38.66) * mm});
            skLineSegment(sketch, "E185", {"start": v(-9.9, -38.66) * mm, "end": v(-9.9, -17.26) * mm});
            skFitSpline(sketch, "E186", {"points": [v(38.66, -9.9) * mm, v(35.07, -23.98) * mm, v(23.98, -35.07) * mm, v(9.9, -38.66) * mm]});
            skLineSegment(sketch, "E187", {"start": v(17.26, -9.9) * mm, "end": v(38.66, -9.9) * mm});
            skLineSegment(sketch, "E188", {"start": v(38.66, -9.9) * mm, "end": v(17.26, -9.9) * mm});
            skFitSpline(sketch, "E189", {"points": [v(9.9, -17.26) * mm, v(12.96, -15.5) * mm, v(15.5, -12.96) * mm, v(17.26, -9.9) * mm]});
            skLineSegment(sketch, "E190", {"start": v(9.9, -38.66) * mm, "end": v(9.9, -17.26) * mm});
            skLineSegment(sketch, "E191", {"start": v(9.9, -17.26) * mm, "end": v(9.9, -38.66) * mm});
            skSolve(sketch);
        }
        {
            var Q0;
            Q0 = qSketchRegion(id + "F4", true);
            var Q1;
            Q1=makeQuery(id+"F1.opExtrude","CAP_FACE",FACE,{"disambiguationData":[OSD([sQuery(id+"F0.wireOp",EDGE,"E0"),sQuery(id+"F0.wireOp",EDGE,"E1"),sQuery(id+"F0.wireOp",EDGE,"E2"),sQuery(id+"F0.wireOp",EDGE,"E3"),sQuery(id+"F0.wireOp",EDGE,"E4"),sQuery(id+"F0.wireOp",EDGE,"E5"),sQuery(id+"F0.wireOp",EDGE,"E6"),sQuery(id+"F0.wireOp",EDGE,"E7"),sQuery(id+"F0.wireOp",EDGE,"E8"),sQuery(id+"F0.wireOp",EDGE,"E9"),sQuery(id+"F0.wireOp",EDGE,"E10"),sQuery(id+"F0.wireOp",EDGE,"E11"),sQuery(id+"F0.wireOp",EDGE,"E12"),sQuery(id+"F0.wireOp",EDGE,"E13"),sQuery(id+"F0.wireOp",EDGE,"E14"),sQuery(id+"F0.wireOp",EDGE,"E15"),sQuery(id+"F0.wireOp",EDGE,"E16"),sQuery(id+"F0.wireOp",EDGE,"E17"),sQuery(id+"F0.wireOp",EDGE,"E18"),sQuery(id+"F0.wireOp",EDGE,"E19"),sQuery(id+"F0.wireOp",EDGE,"E20"),sQuery(id+"F0.wireOp",EDGE,"E21"),sQuery(id+"F0.wireOp",EDGE,"E22"),sQuery(id+"F0.wireOp",EDGE,"E23"),sQuery(id+"F0.wireOp",EDGE,"E24"),sQuery(id+"F0.wireOp",EDGE,"E25"),sQuery(id+"F0.wireOp",EDGE,"E26"),sQuery(id+"F0.wireOp",EDGE,"E27"),sQuery(id+"F0.wireOp",EDGE,"E28"),sQuery(id+"F0.wireOp",EDGE,"E29"),sQuery(id+"F0.wireOp",EDGE,"E30"),sQuery(id+"F0.wireOp",EDGE,"E31"),sQuery(id+"F0.wireOp",EDGE,"E32"),sQuery(id+"F0.wireOp",EDGE,"E33"),sQuery(id+"F0.wireOp",EDGE,"E34"),sQuery(id+"F0.wireOp",EDGE,"E35"),sQuery(id+"F0.wireOp",EDGE,"E36"),sQuery(id+"F0.wireOp",EDGE,"E37"),sQuery(id+"F0.wireOp",EDGE,"E38"),sQuery(id+"F0.wireOp",EDGE,"E39"),sQuery(id+"F0.wireOp",EDGE,"E40"),sQuery(id+"F0.wireOp",EDGE,"E41"),sQuery(id+"F0.wireOp",EDGE,"E42"),sQuery(id+"F0.wireOp",EDGE,"E43"),sQuery(id+"F0.wireOp",EDGE,"E44"),sQuery(id+"F0.wireOp",EDGE,"E45"),sQuery(id+"F0.wireOp",EDGE,"E46"),sQuery(id+"F0.wireOp",EDGE,"E47"),sQuery(id+"F0.wireOp",EDGE,"E48"),sQuery(id+"F0.wireOp",EDGE,"E49"),sQuery(id+"F0.wireOp",EDGE,"E50"),sQuery(id+"F0.wireOp",EDGE,"E51"),sQuery(id+"F0.wireOp",EDGE,"E52"),sQuery(id+"F0.wireOp",EDGE,"E53"),sQuery(id+"F0.wireOp",EDGE,"E54"),sQuery(id+"F0.wireOp",EDGE,"E55"),sQuery(id+"F0.wireOp",EDGE,"E56"),sQuery(id+"F0.wireOp",EDGE,"E57"),sQuery(id+"F0.wireOp",EDGE,"E58"),sQuery(id+"F0.wireOp",EDGE,"E59"),sQuery(id+"F0.wireOp",EDGE,"E60"),sQuery(id+"F0.wireOp",EDGE,"E61"),sQuery(id+"F0.wireOp",EDGE,"E62"),sQuery(id+"F0.wireOp",EDGE,"E63"),sQuery(id+"F0.wireOp",EDGE,"E64"),sQuery(id+"F0.wireOp",EDGE,"E65"),sQuery(id+"F0.wireOp",EDGE,"E66"),sQuery(id+"F0.wireOp",EDGE,"E67"),sQuery(id+"F0.wireOp",EDGE,"E68"),sQuery(id+"F0.wireOp",EDGE,"E69"),sQuery(id+"F0.wireOp",EDGE,"E70"),sQuery(id+"F0.wireOp",EDGE,"E71"),sQuery(id+"F0.wireOp",EDGE,"E72"),sQuery(id+"F0.wireOp",EDGE,"E73"),sQuery(id+"F0.wireOp",EDGE,"E74"),sQuery(id+"F0.wireOp",EDGE,"E75"),sQuery(id+"F0.wireOp",EDGE,"E76"),sQuery(id+"F0.wireOp",EDGE,"E77"),sQuery(id+"F0.wireOp",EDGE,"E78"),sQuery(id+"F0.wireOp",EDGE,"E79"),sQuery(id+"F0.wireOp",EDGE,"E80"),sQuery(id+"F0.wireOp",EDGE,"E81"),sQuery(id+"F0.wireOp",EDGE,"E82"),sQuery(id+"F0.wireOp",EDGE,"E83"),sQuery(id+"F0.wireOp",EDGE,"E84"),sQuery(id+"F0.wireOp",EDGE,"E85"),sQuery(id+"F0.wireOp",EDGE,"E86"),sQuery(id+"F0.wireOp",EDGE,"E87"),sQuery(id+"F0.wireOp",EDGE,"E88"),sQuery(id+"F0.wireOp",EDGE,"E89"),sQuery(id+"F0.wireOp",EDGE,"E90"),sQuery(id+"F0.wireOp",EDGE,"E91"),sQuery(id+"F0.wireOp",EDGE,"E92"),sQuery(id+"F0.wireOp",EDGE,"E93"),sQuery(id+"F0.wireOp",EDGE,"E94"),sQuery(id+"F0.wireOp",EDGE,"E95"),sQuery(id+"F0.wireOp",EDGE,"E96"),sQuery(id+"F0.wireOp",EDGE,"E97"),sQuery(id+"F0.wireOp",EDGE,"E98"),sQuery(id+"F0.wireOp",EDGE,"E99"),sQuery(id+"F0.wireOp",EDGE,"E100"),sQuery(id+"F0.wireOp",EDGE,"E101"),sQuery(id+"F0.wireOp",EDGE,"E102"),sQuery(id+"F0.wireOp",EDGE,"E103"),sQuery(id+"F0.wireOp",EDGE,"E104"),sQuery(id+"F0.wireOp",EDGE,"E105"),sQuery(id+"F0.wireOp",EDGE,"E106"),sQuery(id+"F0.wireOp",EDGE,"E107"),sQuery(id+"F0.wireOp",EDGE,"E108"),sQuery(id+"F0.wireOp",EDGE,"E109"),sQuery(id+"F0.wireOp",EDGE,"E110"),sQuery(id+"F0.wireOp",EDGE,"E111"),sQuery(id+"F0.wireOp",EDGE,"E112"),sQuery(id+"F0.wireOp",EDGE,"E113"),sQuery(id+"F0.wireOp",EDGE,"E114"),sQuery(id+"F0.wireOp",EDGE,"E115"),sQuery(id+"F0.wireOp",EDGE,"E116"),sQuery(id+"F0.wireOp",EDGE,"E117"),sQuery(id+"F0.wireOp",EDGE,"E118"),sQuery(id+"F0.wireOp",EDGE,"E119"),sQuery(id+"F0.wireOp",EDGE,"E120"),sQuery(id+"F0.wireOp",EDGE,"E121"),sQuery(id+"F0.wireOp",EDGE,"E122"),sQuery(id+"F0.wireOp",EDGE,"E123"),sQuery(id+"F0.wireOp",EDGE,"E124"),sQuery(id+"F0.wireOp",EDGE,"E125"),sQuery(id+"F0.wireOp",EDGE,"E126"),sQuery(id+"F0.wireOp",EDGE,"E127"),sQuery(id+"F0.wireOp",EDGE,"E128"),sQuery(id+"F0.wireOp",EDGE,"E129"),sQuery(id+"F0.wireOp",EDGE,"E130"),sQuery(id+"F0.wireOp",EDGE,"E131"),sQuery(id+"F0.wireOp",EDGE,"E132"),sQuery(id+"F0.wireOp",EDGE,"E133"),sQuery(id+"F0.wireOp",EDGE,"E134"),sQuery(id+"F0.wireOp",EDGE,"E135"),sQuery(id+"F0.wireOp",EDGE,"E136"),sQuery(id+"F0.wireOp",EDGE,"E137"),sQuery(id+"F0.wireOp",EDGE,"E138"),sQuery(id+"F0.wireOp",EDGE,"E139"),sQuery(id+"F0.wireOp",EDGE,"E140"),sQuery(id+"F0.wireOp",EDGE,"E141"),sQuery(id+"F0.wireOp",EDGE,"E142"),sQuery(id+"F0.wireOp",EDGE,"E143"),sQuery(id+"F0.wireOp",EDGE,"E144"),sQuery(id+"F0.wireOp",EDGE,"E145"),sQuery(id+"F0.wireOp",EDGE,"E146"),sQuery(id+"F0.wireOp",EDGE,"E147"),sQuery(id+"F0.wireOp",EDGE,"E148"),sQuery(id+"F0.wireOp",EDGE,"E149"),sQuery(id+"F0.wireOp",EDGE,"E150"),sQuery(id+"F0.wireOp",EDGE,"E151"),sQuery(id+"F0.wireOp",EDGE,"E152"),sQuery(id+"F0.wireOp",EDGE,"E153"),sQuery(id+"F0.wireOp",EDGE,"E154"),sQuery(id+"F0.wireOp",EDGE,"E155"),sQuery(id+"F0.wireOp",EDGE,"E156"),sQuery(id+"F0.wireOp",EDGE,"E157"),sQuery(id+"F0.wireOp",EDGE,"E158"),sQuery(id+"F0.wireOp",EDGE,"E159")])],"isStart":true});
            extrude(context, id + "F5", {"entities" : qUnion([Q0]), "operationType" : NewBodyOperationType.REMOVE, "endBound" : BoundingType.UP_TO_SURFACE, "oppositeDirection" : true, "endBoundEntityFace" : qUnion([Q1]), "depth" : 25 * mm});
        }
    });
